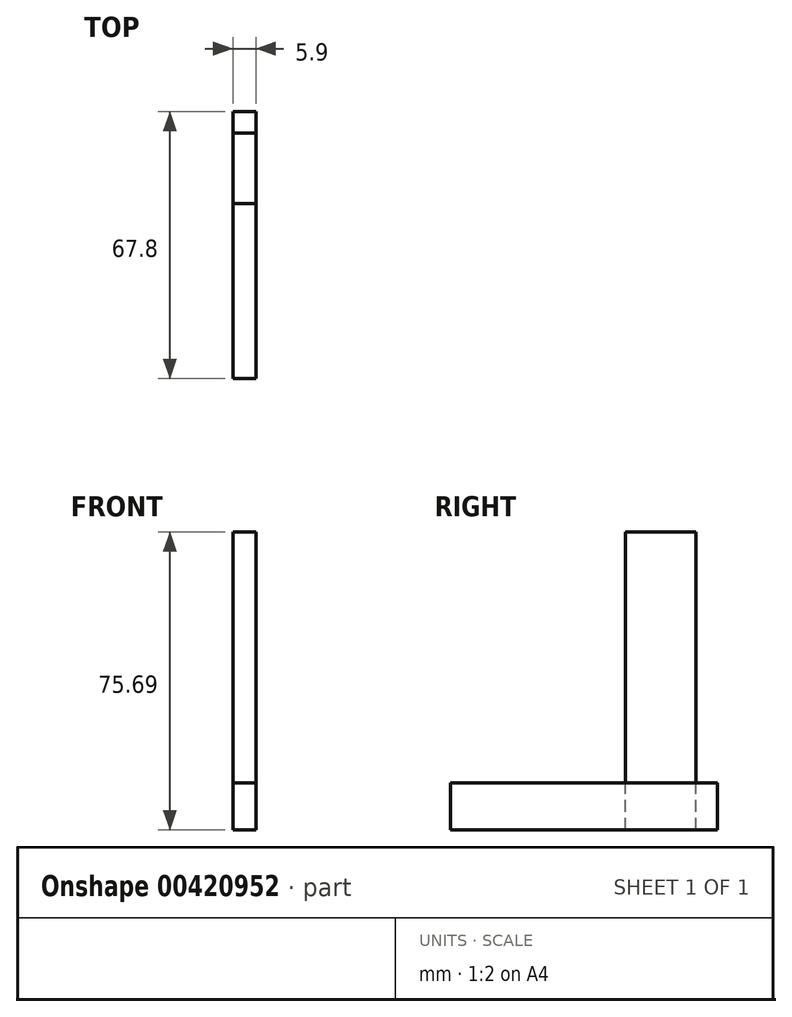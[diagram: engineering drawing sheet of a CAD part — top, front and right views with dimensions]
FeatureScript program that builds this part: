
annotation { "Feature Type Name" : "Feature", "Feature Type Description" : "" }
export const myFeature = defineFeature(function(context is Context, id is Id, definition is map)
    precondition{}
    {
        {
            var Q0;
            Q0=qCreatedBy(makeId("Top.planeOp"),FACE);
            var sketch = newSketch(context, id + "F0", { "sketchPlane" : qUnion([Q0])});
            skLineSegment(sketch, "E0", {"start": v(0, 0) * mm, "end": v(0, -23.22) * mm});
            skLineSegment(sketch, "E1", {"start": v(-4.35, -27.57) * mm, "end": v(-45.13, -27.57) * mm});
            skLineSegment(sketch, "E2", {"start": v(-49.48, -23.22) * mm, "end": v(-49.48, 0) * mm});
            skPoint(sketch, "E3.visualSharp", {"position": v(0, -27.57) * mm});
            skArc(sketch, "E3.filletArc", {"start": v(-4.35, -27.57) * mm, "mid": v(-1.27, -26.3) * mm, "end": v(0, -23.22) * mm});
            skPoint(sketch, "E4.visualSharp", {"position": v(-49.48, -27.57) * mm});
            skArc(sketch, "E4.filletArc", {"start": v(-49.48, -23.22) * mm, "mid": v(-48.2, -26.3) * mm, "end": v(-45.13, -27.57) * mm});
            skSolve(sketch);
        }
        {
            var Q0;
            Q0=qCreatedBy(makeId("Front.planeOp"),FACE);
            var sketch = newSketch(context, id + "F1", { "sketchPlane" : qUnion([Q0])});
            skLineSegment(sketch, "E5.bottom", {"start": v(0, 0) * mm, "end": v(6.07, 0) * mm});
            skLineSegment(sketch, "E5.top", {"start": v(0, 11.68) * mm, "end": v(6.07, 11.68) * mm});
            skLineSegment(sketch, "E5.left", {"start": v(0, 0) * mm, "end": v(0, 11.68) * mm});
            skLineSegment(sketch, "E5.right", {"start": v(6.07, 0) * mm, "end": v(6.07, 11.68) * mm});
            skSolve(sketch);
        }
        {
            var Q0;
            Q0=qCreatedBy(makeId("Top.planeOp"),FACE);
            var sketch = newSketch(context, id + "F2", { "sketchPlane" : qUnion([Q0])});
            skLineSegment(sketch, "E6.bottom", {"start": v(6.11, 0) * mm, "end": v(12, 0) * mm});
            skLineSegment(sketch, "E6.top", {"start": v(6.11, -67.8) * mm, "end": v(12, -67.8) * mm});
            skLineSegment(sketch, "E6.left", {"start": v(6.11, 0) * mm, "end": v(6.11, -67.8) * mm});
            skLineSegment(sketch, "E6.right", {"start": v(12, 0) * mm, "end": v(12, -67.8) * mm});
            skSolve(sketch);
        }
        {
            var Q0;
            Q0=makeQuery(id+"F2.imprint","IMPRINT",FACE,{"disambiguationData":[TD([[makeQuery(id+"F2.imprint","IMPRINT",EDGE,{"derivedFrom":sQuery(id+"F2.wireOp",EDGE,"E6.bottom")}),-1.0]])]});
            extrude(context, id + "F3", {"entities" : qUnion([Q0]), "depth" : 11.94 * mm});
        }
        {
            var Q0;
            Q0=qCreatedBy(makeId("Top.planeOp"),FACE);
            var sketch = newSketch(context, id + "F4", { "sketchPlane" : qUnion([Q0])});
            skLineSegment(sketch, "E7.bottom", {"start": v(6.1, -23.3) * mm, "end": v(11.97, -23.3) * mm});
            skLineSegment(sketch, "E7.top", {"start": v(6.1, -5.41) * mm, "end": v(11.97, -5.41) * mm});
            skLineSegment(sketch, "E7.left", {"start": v(6.1, -23.3) * mm, "end": v(6.1, -5.41) * mm});
            skLineSegment(sketch, "E7.right", {"start": v(11.97, -23.3) * mm, "end": v(11.97, -5.41) * mm});
            skSolve(sketch);
        }
        {
            var Q0;
            Q0=makeQuery(id+"F4.imprint","IMPRINT",FACE,{"disambiguationData":[TD([[makeQuery(id+"F4.imprint","IMPRINT",EDGE,{"derivedFrom":sQuery(id+"F4.wireOp",EDGE,"E7.bottom")}),1.0]])]});
            extrude(context, id + "F5", {"entities" : qUnion([Q0]), "operationType" : NewBodyOperationType.ADD, "depth" : 75.7 * mm});
        }
    });
